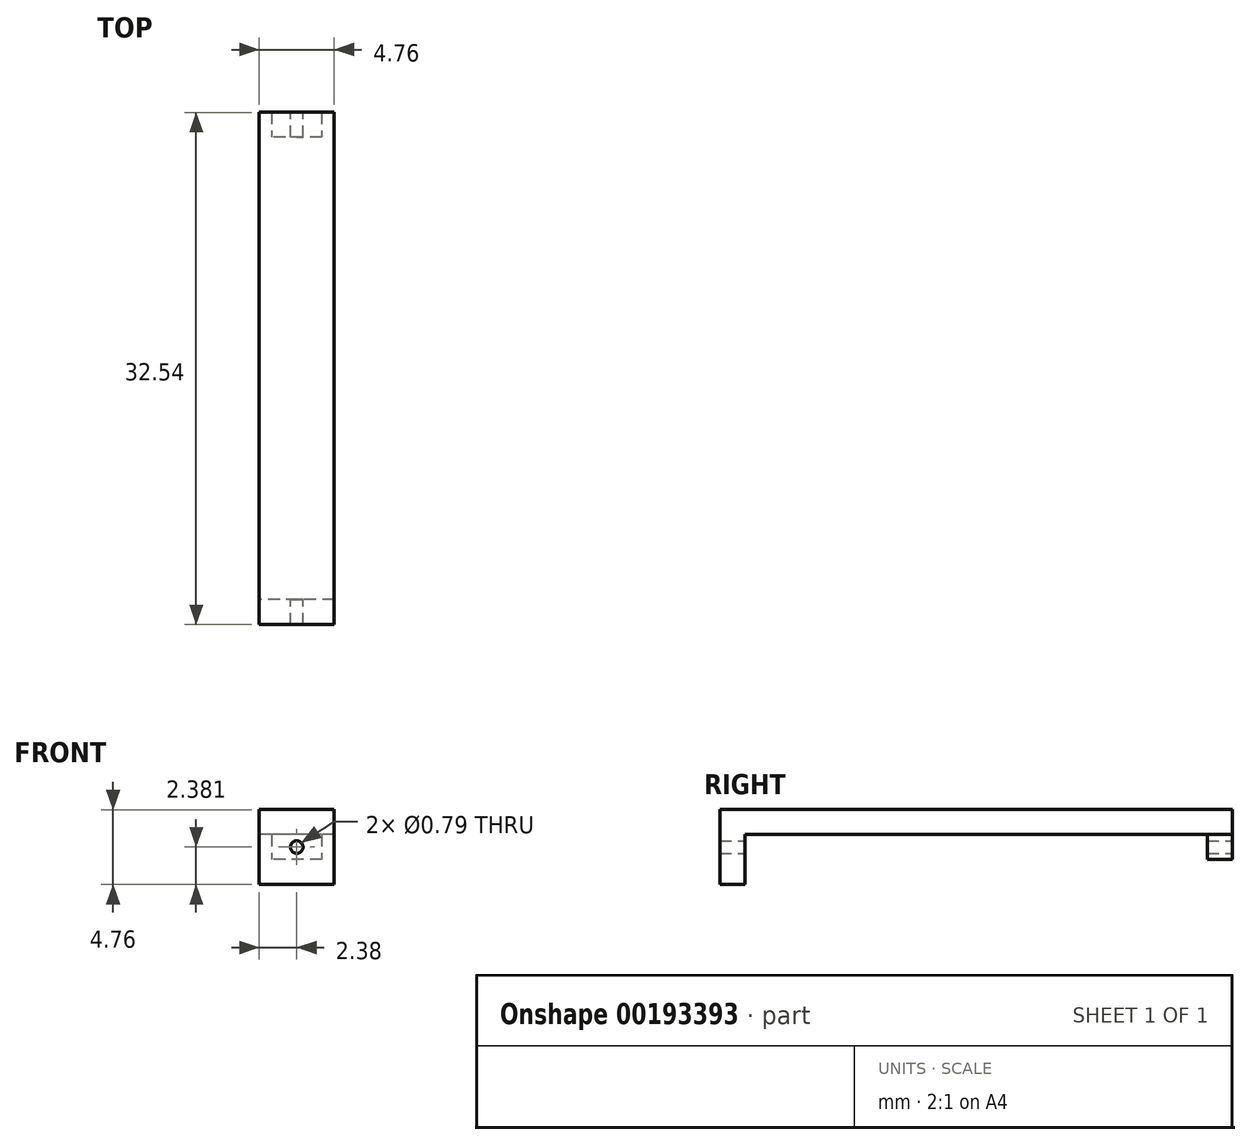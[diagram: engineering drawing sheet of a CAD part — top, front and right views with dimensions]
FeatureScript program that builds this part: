
annotation { "Feature Type Name" : "Feature", "Feature Type Description" : "" }
export const myFeature = defineFeature(function(context is Context, id is Id, definition is map)
    precondition{}
    {
        {
            var Q0;
            Q0=qCreatedBy(makeId("Top.planeOp"),FACE);
            var sketch = newSketch(context, id + "F0", { "sketchPlane" : qUnion([Q0])});
            skLineSegment(sketch, "E0.bottom", {"start": v(2.38, 16.27) * mm, "end": v(-2.38, 16.27) * mm});
            skLineSegment(sketch, "E0.top", {"start": v(2.38, -16.27) * mm, "end": v(-2.38, -16.27) * mm});
            skLineSegment(sketch, "E0.left", {"start": v(2.38, 16.27) * mm, "end": v(2.38, -16.27) * mm});
            skLineSegment(sketch, "E0.right", {"start": v(-2.38, 16.27) * mm, "end": v(-2.38, -16.27) * mm});
            skPoint(sketch, "E0.middle", {"position": v(0, 0) * mm});
            skSolve(sketch);
        }
        {
            var Q0;
            Q0 = qSketchRegion(id + "F0", true);
            extrude(context, id + "F1", {"entities" : qUnion([Q0]), "depth" : 4.76 * mm});
        }
        {
            var Q0;
            Q0=makeQuery(id+"F1.opExtrude","CAP_FACE",FACE,{"disambiguationData":[OSD([sQuery(id+"F0.wireOp",EDGE,"E0.bottom"),sQuery(id+"F0.wireOp",EDGE,"E0.top"),sQuery(id+"F0.wireOp",EDGE,"E0.left"),sQuery(id+"F0.wireOp",EDGE,"E0.right")])],"isStart":true});
            var sketch = newSketch(context, id + "F2", { "sketchPlane" : qUnion([Q0])});
            skLineSegment(sketch, "E1.bottom", {"start": v(2.38, 14.68) * mm, "end": v(-2.38, 14.68) * mm});
            skLineSegment(sketch, "E1.top", {"start": v(2.38, -16.27) * mm, "end": v(1.59, -16.27) * mm});
            skLineSegment(sketch, "E1.left", {"start": v(2.38, 14.68) * mm, "end": v(2.38, -16.27) * mm});
            skLineSegment(sketch, "E1.right", {"start": v(-2.38, 14.68) * mm, "end": v(-2.38, -16.27) * mm});
            skLineSegment(sketch, "E2.top", {"start": v(1.59, -14.68) * mm, "end": v(-1.59, -14.68) * mm});
            skLineSegment(sketch, "E2.left", {"start": v(1.59, -16.27) * mm, "end": v(1.59, -14.68) * mm});
            skLineSegment(sketch, "E2.right", {"start": v(-1.59, -16.27) * mm, "end": v(-1.59, -14.68) * mm});
            skLineSegment(sketch, "E3.trimOffspring", {"start": v(-1.59, -16.27) * mm, "end": v(-2.38, -16.27) * mm});
            skSolve(sketch);
        }
        {
            var Q0;
            Q0 = qSketchRegion(id + "F2", true);
            extrude(context, id + "F3", {"entities" : qUnion([Q0]), "operationType" : NewBodyOperationType.REMOVE, "oppositeDirection" : true, "depth" : 3.17 * mm});
        }
        {
            var Q0;
            {var subQ0=sQuery(id+"F0.wireOp",EDGE,"E0.bottom");Q0=makeQuery(id+"F3.boolean.opBoolean","SPLIT",FACE,{"disambiguationData":[TD([makeQuery(id+"F1.opExtrude","SWEPT_FACE",FACE,{"disambiguationData":[OSD([subQ0])]})])],"derivedFrom":makeQuery(id+"F1.opExtrude","CAP_FACE",FACE,{"disambiguationData":[OSD([subQ0,sQuery(id+"F0.wireOp",EDGE,"E0.top"),sQuery(id+"F0.wireOp",EDGE,"E0.left"),sQuery(id+"F0.wireOp",EDGE,"E0.right")])],"isStart":true})});}
            extrude(context, id + "F4", {"entities" : qUnion([Q0]), "operationType" : NewBodyOperationType.REMOVE, "oppositeDirection" : true, "depth" : 1.59 * mm});
        }
        {
            var Q0;
            Q0=makeQuery(id+"F1.opExtrude","SWEPT_FACE",FACE,{"disambiguationData":[OSD([sQuery(id+"F0.wireOp",EDGE,"E0.bottom")])]});
            var sketch = newSketch(context, id + "F5", { "sketchPlane" : qUnion([Q0])});
            skPoint(sketch, "E4.positionSnap0", {"position": v(0, 1.59) * mm});
            skPoint(sketch, "E4.positionSnap1", {"position": v(-1.59, 2.38) * mm});
            skCircle(sketch, "E5", {"center": v(0, 2.38) * mm, "radius": 0.4 * mm});
            skSolve(sketch);
        }
        {
            var Q0;
            Q0 = qSketchRegion(id + "F5", true);
            extrude(context, id + "F6", {"entities" : qUnion([Q0]), "operationType" : NewBodyOperationType.REMOVE, "endBound" : BoundingType.THROUGH_ALL, "oppositeDirection" : true, "depth" : 25.4 * mm});
        }
    });
